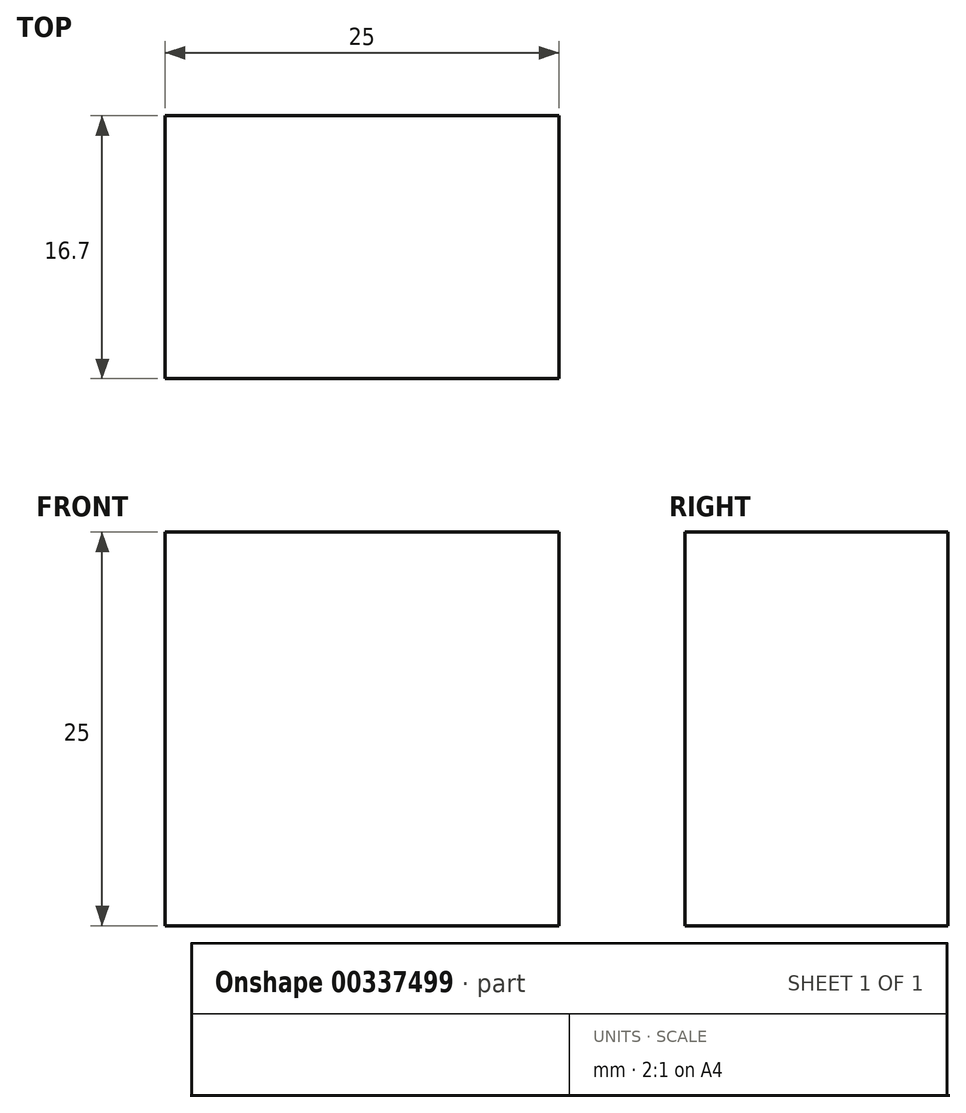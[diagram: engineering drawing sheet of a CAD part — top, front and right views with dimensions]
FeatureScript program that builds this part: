
annotation { "Feature Type Name" : "Feature", "Feature Type Description" : "" }
export const myFeature = defineFeature(function(context is Context, id is Id, definition is map)
    precondition{}
    {
        {
            var Q0;
            Q0=qCreatedBy(makeId("Front.planeOp"),FACE);
            var sketch = newSketch(context, id + "F0", { "sketchPlane" : qUnion([Q0])});
            skLineSegment(sketch, "E0.bottom", {"start": v(-12.9, 12.65) * mm, "end": v(12.1, 12.65) * mm});
            skLineSegment(sketch, "E0.top", {"start": v(-12.9, -12.35) * mm, "end": v(12.1, -12.35) * mm});
            skLineSegment(sketch, "E0.left", {"start": v(-12.9, 12.65) * mm, "end": v(-12.9, -12.35) * mm});
            skLineSegment(sketch, "E0.right", {"start": v(12.1, 12.65) * mm, "end": v(12.1, -12.35) * mm});
            skSolve(sketch);
        }
        {
            var Q0;
            Q0 = qSketchRegion(id + "F0", true);
            extrude(context, id + "F1", {"entities" : qUnion([Q0]), "depth" : 16.7 * mm});
        }
    });
